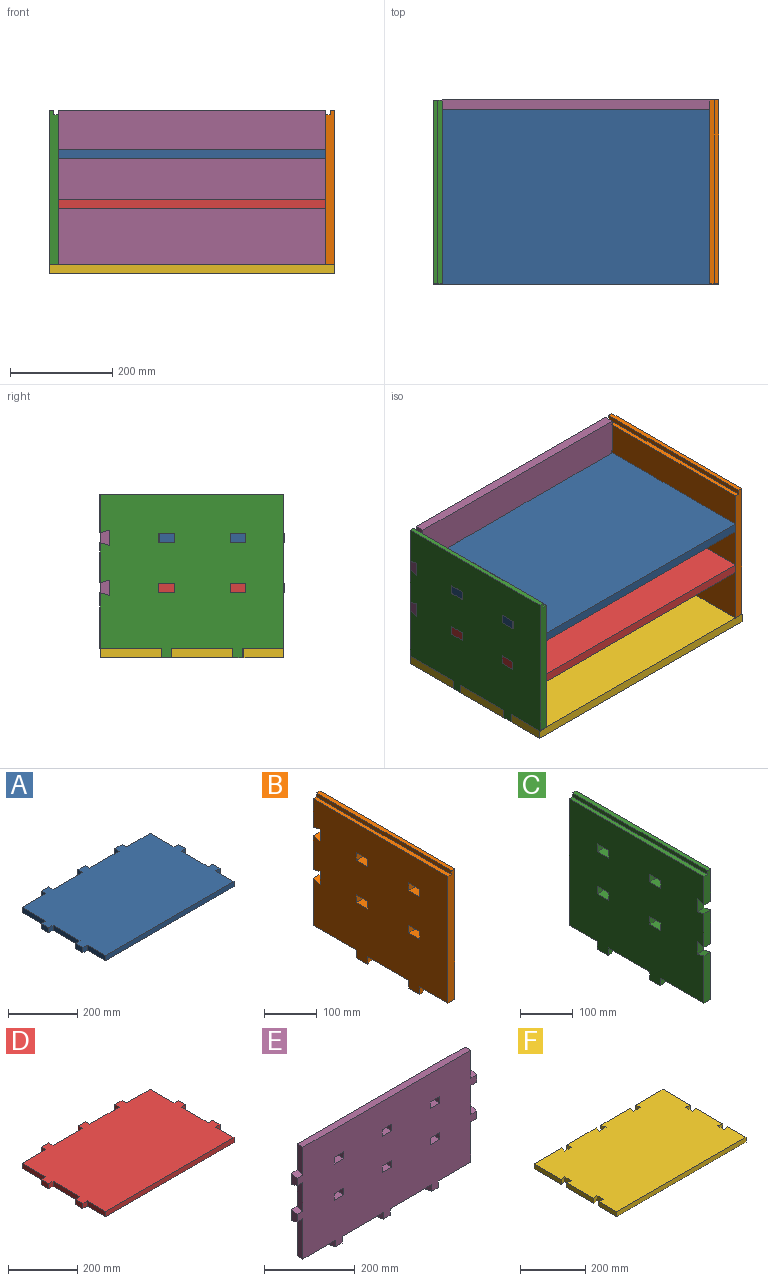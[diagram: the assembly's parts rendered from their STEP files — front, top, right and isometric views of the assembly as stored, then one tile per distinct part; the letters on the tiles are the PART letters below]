
ASSEMBLY  parts=6 mates=5
PART A: 34 faces, bbox 560x360.5x18 mm
  f0: plane 30x18mm, normal (0,1,0), area 540mm2, adj f1,f31,f32,f33
  f1: plane 18x18mm, normal (-1,0,0), area 324mm2, adj f0,f2,f32,f33
  f2: plane 120x18mm, normal (0,1,0), area 2160mm2, adj f1,f3,f32,f33
  f3: plane 18x18mm, normal (1,0,0), area 324mm2, adj f2,f4,f32,f33
  f4: plane 30x18mm, normal (0,1,0), area 540mm2, adj f3,f5,f32,f33
  f5: plane 18x18mm, normal (-1,0,0), area 324mm2, adj f4,f6,f32,f33
  f6: plane 97x18mm, normal (0,1,0), area 1746mm2, adj f5,f7,f32,f33
  f7: plane 97x18mm, normal (-1,0,0), area 1746mm2, adj f6,f8,f32,f33
  f8: plane 18x18mm, normal (0,1,0), area 324mm2, adj f7,f9,f32,f33
  f9: plane 30x18mm, normal (-1,0,0), area 540mm2, adj f8,f10,f32,f33
  f10: plane 18x18mm, normal (0,-1,0), area 324mm2, adj f9,f11,f32,f33
  f11: plane 110x18mm, normal (-1,0,0), area 1980mm2, adj f10,f12,f32,f33
  f12: plane 18x18mm, normal (0,1,0), area 324mm2, adj f11,f13,f32,f33
  f13: plane 30x18mm, normal (-1,0,0), area 540mm2, adj f12,f14,f32,f33
  f14: plane 18x18mm, normal (0,-1,0), area 324mm2, adj f13,f15,f32,f33
  f15: plane 75x18mm, normal (-1,0,0), area 1350mm2, adj f14,f16,f32,f33
  f16: plane 524x18mm, normal (0,-1,0), area 9432mm2, adj f15,f17,f32,f33
  f17: plane 75x18mm, normal (1,0,0), area 1350mm2, adj f16,f18,f32,f33
  f18: plane 18x18mm, normal (0,-1,0), area 324mm2, adj f17,f19,f32,f33
  f19: plane 30.58x18mm, normal (1,0,0), area 550.4mm2, adj f18,f20,f32,f33
  f20: plane 18x18mm, normal (0,1,0), area 324mm2, adj f19,f21,f32,f33
  f21: plane 110x18mm, normal (1,0,0), area 1980mm2, adj f20,f22,f32,f33
  f22: plane 18x18mm, normal (0,-1,0), area 324mm2, adj f21,f23,f32,f33
  f23: plane 29.42x18mm, normal (1,0,0), area 529.6mm2, adj f22,f24,f32,f33
  f24: plane 18x18mm, normal (0,1,0), area 324mm2, adj f23,f25,f32,f33
  f25: plane 97x18mm, normal (1,0,0), area 1746mm2, adj f24,f26,f32,f33
  f26: plane 97x18mm, normal (0,1,0), area 1746mm2, adj f25,f27,f32,f33
  f27: plane 18x18mm, normal (1,0,0), area 324mm2, adj f26,f28,f32,f33
  f28: plane 30x18mm, normal (0,1,0), area 540mm2, adj f27,f29,f32,f33
  f29: plane 18x17.51mm, normal (-1,0,0), area 315.2mm2, adj f28,f30,f32,f33
  f30: plane 120x18mm, normal (0,1,0), area 2160mm2, adj f29,f31,f32,f33
  f31: plane 18x18mm, normal (1,0,0), area 324mm2, adj f0,f30,f32,f33
  f32: plane 560x360.49mm, normal (0,0,1), area 183091.1mm2, adj f0,f1,f2,f3,f4,f5,f6,f7
  f33: plane 560x360.49mm, normal (0,0,-1), area 183091.1mm2, adj f0,f1,f2,f3,f4,f5,f6,f7
PART B: 40 faces, bbox 18x360x320 mm
  f0: plane 360x320mm, normal (1,0,0), area 106380mm2, adj f1,f3,f4,f5,f6,f7,f8,f9
  f1: plane 18x18mm, normal (0.27,0.96,0), area 336.3mm2, adj f0,f2,f4,f5
  f2: plane 360x311mm, normal (-1,0,0), area 103500mm2, adj f1,f3,f4,f5,f6,f7,f8,f9
  f3: plane 18x18mm, normal (0.27,-0.96,0), area 336.3mm2, adj f0,f2,f4,f9
  f4: plane 30x18mm, normal (0,0,-1), area 450mm2, adj f0,f1,f2,f3
  f5: plane 120x18mm, normal (0,0,-1), area 2115mm2, adj f0,f1,f2,f15
  f6: plane 18x18mm, normal (0.27,-0.96,0), area 336.3mm2, adj f0,f2,f8,f14
  f7: plane 18x18mm, normal (0.27,0.96,0), area 336.3mm2, adj f0,f2,f8,f9
  f8: plane 30x18mm, normal (0,0,-1), area 450mm2, adj f0,f2,f6,f7
  f9: plane 120x18mm, normal (0,0,-1), area 2070mm2, adj f0,f2,f3,f7
  f10: plane 360x9mm, normal (0,0,1), area 3240mm2, adj f0,f23,f33,f39
  f11: plane 18x18mm, normal (0,1,0), area 324mm2, adj f0,f2,f12,f37
  f12: plane 30x18mm, normal (0,0,-1), area 540mm2, adj f0,f2,f11,f13
  f13: plane 18x18mm, normal (0,-1,0), area 324mm2, adj f0,f2,f12,f37
  f14: plane 80x18mm, normal (0,0,-1), area 1395mm2, adj f0,f2,f6,f33
  f15: plane 109x18mm, normal (0,1,0), area 1962mm2, adj f0,f2,f5,f16
  f16: plane 18x18mm, normal (0,-0.27,0.96), area 336.3mm2, adj f0,f2,f15,f17
  f17: plane 30x18mm, normal (0,1,0), area 540mm2, adj f0,f2,f16,f18
  f18: plane 18x18mm, normal (0,-0.27,-0.96), area 336.3mm2, adj f0,f2,f17,f19
  f19: plane 78x18mm, normal (0,1,0), area 1404mm2, adj f0,f2,f18,f20
  f20: plane 18x18mm, normal (0,-0.27,0.96), area 336.3mm2, adj f0,f2,f19,f21
  f21: plane 30x18mm, normal (0,1,0), area 540mm2, adj f0,f2,f20,f22
  f22: plane 18x18mm, normal (0,-0.27,-0.96), area 336.3mm2, adj f0,f2,f21,f23
  f23: plane 75x18mm, normal (0,1,0), area 1269mm2, adj f0,f2,f10,f22,f38,f39
  f24: plane 18x18mm, normal (0,1,0), area 324mm2, adj f0,f2,f25,f34
  f25: plane 30x18mm, normal (0,0,-1), area 540mm2, adj f0,f2,f24,f26
  f26: plane 18x18mm, normal (0,-1,0), area 324mm2, adj f0,f2,f25,f34
  f27: plane 30x18mm, normal (0,0,1), area 540mm2, adj f0,f2,f28,f35
  f28: plane 18x18mm, normal (0,1,0), area 324mm2, adj f0,f2,f27,f29
  f29: plane 30x18mm, normal (0,0,-1), area 540mm2, adj f0,f2,f28,f35
  f30: plane 30x18mm, normal (0,0,-1), area 540mm2, adj f0,f2,f31,f36
  f31: plane 18x18mm, normal (0,-1,0), area 324mm2, adj f0,f2,f30,f32
  f32: plane 30x18mm, normal (0,0,1), area 540mm2, adj f0,f2,f31,f36
  f33: plane 302x18mm, normal (0,-1,0), area 5355mm2, adj f0,f2,f10,f14,f38,f39
  f34: plane 30x18mm, normal (0,0,1), area 540mm2, adj f0,f2,f24,f26
  f35: plane 18x18mm, normal (0,-1,0), area 324mm2, adj f0,f2,f27,f29
  f36: plane 18x18mm, normal (0,1,0), area 324mm2, adj f0,f2,f30,f32
  f37: plane 30x18mm, normal (0,0,1), area 540mm2, adj f0,f2,f11,f13
  f38: plane 360x9mm, normal (0,0,1), area 3240mm2, adj f2,f23,f33,f39
  f39: plane 360x9mm, normal (-1,0,0), area 3240mm2, adj f10,f23,f33,f38
PART C: 40 faces, bbox 18x360x320 mm
  f0: plane 360x320mm, normal (1,0,0), area 106380mm2, adj f1,f3,f4,f5,f6,f7,f8,f9
  f1: plane 18x18mm, normal (0.27,0.96,0), area 336.3mm2, adj f0,f2,f4,f5
  f2: plane 360x311mm, normal (-1,0,0), area 103500mm2, adj f1,f3,f4,f5,f6,f7,f8,f9
  f3: plane 18x18mm, normal (0.27,-0.96,0), area 336.3mm2, adj f0,f2,f4,f9
  f4: plane 30x18mm, normal (0,0,-1), area 450mm2, adj f0,f1,f2,f3
  f5: plane 80x18mm, normal (0,0,-1), area 1395mm2, adj f0,f1,f2,f10
  f6: plane 18x18mm, normal (0.27,-0.96,0), area 336.3mm2, adj f0,f2,f8,f19
  f7: plane 18x18mm, normal (0.27,0.96,0), area 336.3mm2, adj f0,f2,f8,f9
  f8: plane 30x18mm, normal (0,0,-1), area 450mm2, adj f0,f2,f6,f7
  f9: plane 120x18mm, normal (0,0,-1), area 2070mm2, adj f0,f2,f3,f7
  f10: plane 302x18mm, normal (0,1,0), area 5355mm2, adj f0,f2,f5,f11,f38,f39
  f11: plane 360x9mm, normal (0,0,1), area 3240mm2, adj f0,f10,f20,f39
  f12: plane 30x18mm, normal (0,-1,0), area 540mm2, adj f0,f2,f13,f37
  f13: plane 18x18mm, normal (0,0.27,0.96), area 336.3mm2, adj f0,f2,f12,f14
  f14: plane 78x18mm, normal (0,-1,0), area 1404mm2, adj f0,f2,f13,f15
  f15: plane 18x18mm, normal (0,0.27,-0.96), area 336.3mm2, adj f0,f2,f14,f16
  f16: plane 30x18mm, normal (0,-1,0), area 540mm2, adj f0,f2,f15,f17
  f17: plane 18x18mm, normal (0,0.27,0.96), area 336.3mm2, adj f0,f2,f16,f18
  f18: plane 109x18mm, normal (0,-1,0), area 1962mm2, adj f0,f2,f17,f19
  f19: plane 120x18mm, normal (0,0,-1), area 2115mm2, adj f0,f2,f6,f18
  f20: plane 75x18mm, normal (0,-1,0), area 1269mm2, adj f0,f2,f11,f37,f38,f39
  f21: plane 18x18mm, normal (0,1,0), area 324mm2, adj f0,f2,f22,f33
  f22: plane 30x18mm, normal (0,0,-1), area 540mm2, adj f0,f2,f21,f23
  f23: plane 18x18mm, normal (0,-1,0), area 324mm2, adj f0,f2,f22,f33
  f24: plane 18x18mm, normal (0,1,0), area 324mm2, adj f0,f2,f25,f34
  f25: plane 30x18mm, normal (0,0,-1), area 540mm2, adj f0,f2,f24,f26
  f26: plane 18x18mm, normal (0,-1,0), area 324mm2, adj f0,f2,f25,f34
  f27: plane 30x18mm, normal (0,0,1), area 540mm2, adj f0,f2,f28,f35
  f28: plane 18x18mm, normal (0,1,0), area 324mm2, adj f0,f2,f27,f29
  f29: plane 30x18mm, normal (0,0,-1), area 540mm2, adj f0,f2,f28,f35
  f30: plane 30x18mm, normal (0,0,-1), area 540mm2, adj f0,f2,f31,f36
  f31: plane 18x18mm, normal (0,-1,0), area 324mm2, adj f0,f2,f30,f32
  f32: plane 30x18mm, normal (0,0,1), area 540mm2, adj f0,f2,f31,f36
  f33: plane 30x18mm, normal (0,0,1), area 540mm2, adj f0,f2,f21,f23
  f34: plane 30x18mm, normal (0,0,1), area 540mm2, adj f0,f2,f24,f26
  f35: plane 18x18mm, normal (0,-1,0), area 324mm2, adj f0,f2,f27,f29
  f36: plane 18x18mm, normal (0,1,0), area 324mm2, adj f0,f2,f30,f32
  f37: plane 18x18mm, normal (0,0.27,-0.96), area 336.3mm2, adj f0,f2,f12,f20
  f38: plane 360x9mm, normal (0,0,1), area 3240mm2, adj f2,f10,f20,f39
  f39: plane 360x9mm, normal (-1,0,0), area 3240mm2, adj f10,f11,f20,f38
PART D: 34 faces, bbox 560x360.5x18 mm
  f0: plane 30x18mm, normal (0,1,0), area 540mm2, adj f1,f31,f32,f33
  f1: plane 18x18mm, normal (-1,0,0), area 324mm2, adj f0,f2,f32,f33
  f2: plane 120x18mm, normal (0,1,0), area 2160mm2, adj f1,f3,f32,f33
  f3: plane 18x18mm, normal (1,0,0), area 324mm2, adj f2,f4,f32,f33
  f4: plane 30x18mm, normal (0,1,0), area 540mm2, adj f3,f5,f32,f33
  f5: plane 18x18mm, normal (-1,0,0), area 324mm2, adj f4,f6,f32,f33
  f6: plane 97x18mm, normal (0,1,0), area 1746mm2, adj f5,f7,f32,f33
  f7: plane 97x18mm, normal (-1,0,0), area 1746mm2, adj f6,f8,f32,f33
  f8: plane 18x18mm, normal (0,1,0), area 324mm2, adj f7,f9,f32,f33
  f9: plane 30x18mm, normal (-1,0,0), area 540mm2, adj f8,f10,f32,f33
  f10: plane 18x18mm, normal (0,-1,0), area 324mm2, adj f9,f11,f32,f33
  f11: plane 110x18mm, normal (-1,0,0), area 1980mm2, adj f10,f12,f32,f33
  f12: plane 18x18mm, normal (0,1,0), area 324mm2, adj f11,f13,f32,f33
  f13: plane 29.99x18mm, normal (-1,0,0), area 539.7mm2, adj f12,f14,f32,f33
  f14: plane 18x18mm, normal (0,-1,0), area 324mm2, adj f13,f15,f32,f33
  f15: plane 75.51x18mm, normal (-1,0,0), area 1359.1mm2, adj f14,f16,f32,f33
  f16: plane 524x18mm, normal (0,-1,0), area 9432mm2, adj f15,f17,f32,f33
  f17: plane 75x18mm, normal (1,0,0), area 1350mm2, adj f16,f18,f32,f33
  f18: plane 18x18mm, normal (0,-1,0), area 324mm2, adj f17,f19,f32,f33
  f19: plane 30.58x18mm, normal (1,0,0), area 550.4mm2, adj f18,f20,f32,f33
  f20: plane 18x18mm, normal (0,1,0), area 324mm2, adj f19,f21,f32,f33
  f21: plane 110x18mm, normal (1,0,0), area 1980mm2, adj f20,f22,f32,f33
  f22: plane 18x18mm, normal (0,-1,0), area 324mm2, adj f21,f23,f32,f33
  f23: plane 29.91x18mm, normal (1,0,0), area 538.4mm2, adj f22,f24,f32,f33
  f24: plane 18x18mm, normal (0,1,0), area 324mm2, adj f23,f25,f32,f33
  f25: plane 97x18mm, normal (1,0,0), area 1746mm2, adj f24,f26,f32,f33
  f26: plane 97x18mm, normal (0,1,0), area 1746mm2, adj f25,f27,f32,f33
  f27: plane 18x18mm, normal (1,0,0), area 324mm2, adj f26,f28,f32,f33
  f28: plane 30x18mm, normal (0,1,0), area 540mm2, adj f27,f29,f32,f33
  f29: plane 18x18mm, normal (-1,0,0), area 324mm2, adj f28,f30,f32,f33
  f30: plane 120x18mm, normal (0,1,0), area 2160mm2, adj f29,f31,f32,f33
  f31: plane 18x18mm, normal (1,0,0), area 324mm2, adj f0,f30,f32,f33
  f32: plane 560x360.49mm, normal (0,0,1), area 183253.8mm2, adj f0,f1,f2,f3,f4,f5,f6,f7
  f33: plane 560x360.49mm, normal (0,0,-1), area 183253.8mm2, adj f0,f1,f2,f3,f4,f5,f6,f7
PART E: 58 faces, bbox 560x18x320 mm
  f0: plane 78x18mm, normal (1,0,0), area 1314mm2, adj f35,f36,f54,f55
  f1: plane 109x18mm, normal (1,0,0), area 1917mm2, adj f8,f35,f36,f56
  f2: plane 78x18mm, normal (-1,0,0), area 1314mm2, adj f35,f36,f46,f49
  f3: plane 109x18mm, normal (-1,0,0), area 1917mm2, adj f4,f35,f36,f50
  f4: plane 102x18mm, normal (0,0,-1), area 1791mm2, adj f3,f35,f36,f43
  f5: plane 130x18mm, normal (0,0,-1), area 2250mm2, adj f35,f36,f38,f40
  f6: plane 130x18mm, normal (0,0,-1), area 2250mm2, adj f35,f36,f37,f44
  f7: plane 75x18mm, normal (-1,0,0), area 1305mm2, adj f34,f35,f36,f47
  f8: plane 102x18mm, normal (0,0,-1), area 1791mm2, adj f1,f35,f36,f41
  f9: plane 75x18mm, normal (1,0,0), area 1305mm2, adj f34,f35,f36,f53
  f10: plane 18x18mm, normal (1,0,0), area 324mm2, adj f11,f28,f35,f36
  f11: plane 30x18mm, normal (0,0,-1), area 540mm2, adj f10,f12,f35,f36
  f12: plane 18x18mm, normal (-1,0,0), area 324mm2, adj f11,f28,f35,f36
  f13: plane 18x18mm, normal (1,0,0), area 324mm2, adj f14,f29,f35,f36
  f14: plane 30x18mm, normal (0,0,-1), area 540mm2, adj f13,f15,f35,f36
  f15: plane 18x18mm, normal (-1,0,0), area 324mm2, adj f14,f29,f35,f36
  f16: plane 18x18mm, normal (1,0,0), area 324mm2, adj f17,f30,f35,f36
  f17: plane 30x18mm, normal (0,0,-1), area 540mm2, adj f16,f18,f35,f36
  f18: plane 18x18mm, normal (-1,0,0), area 324mm2, adj f17,f30,f35,f36
  f19: plane 18x18mm, normal (1,0,0), area 324mm2, adj f20,f31,f35,f36
  f20: plane 30x18mm, normal (0,0,-1), area 540mm2, adj f19,f21,f35,f36
  f21: plane 18x18mm, normal (-1,0,0), area 324mm2, adj f20,f31,f35,f36
  f22: plane 18x18mm, normal (-1,0,0), area 324mm2, adj f23,f32,f35,f36
  f23: plane 30x18mm, normal (0,0,1), area 540mm2, adj f22,f24,f35,f36
  f24: plane 18x18mm, normal (1,0,0), area 324mm2, adj f23,f32,f35,f36
  f25: plane 18x18mm, normal (-1,0,0), area 324mm2, adj f26,f33,f35,f36
  f26: plane 30x18mm, normal (0,0,1), area 540mm2, adj f25,f27,f35,f36
  f27: plane 18x18mm, normal (1,0,0), area 324mm2, adj f26,f33,f35,f36
  f28: plane 30x18mm, normal (0,0,1), area 540mm2, adj f10,f12,f35,f36
  f29: plane 30x18mm, normal (0,0,1), area 540mm2, adj f13,f15,f35,f36
  f30: plane 30x18mm, normal (0,0,1), area 540mm2, adj f16,f18,f35,f36
  f31: plane 30x18mm, normal (0,0,1), area 540mm2, adj f19,f21,f35,f36
  f32: plane 30x18mm, normal (0,0,-1), area 540mm2, adj f22,f24,f35,f36
  f33: plane 30x18mm, normal (0,0,-1), area 540mm2, adj f25,f27,f35,f36
  f34: plane 524x18mm, normal (0,0,1), area 9432mm2, adj f7,f9,f35,f36
  f35: plane 560x320mm, normal (0,-1,0), area 157528mm2, adj f0,f1,f2,f3,f4,f5,f6,f7
  f36: plane 560x320mm, normal (0,1,0), area 158788mm2, adj f0,f1,f2,f3,f4,f5,f6,f7
  f37: plane 18x18mm, normal (-0.96,-0.27,0), area 336.3mm2, adj f6,f35,f36,f39
  f38: plane 18x18mm, normal (0.96,-0.27,0), area 336.3mm2, adj f5,f35,f36,f39
  f39: plane 30x18mm, normal (0,0,-1), area 450mm2, adj f35,f36,f37,f38
  f40: plane 18x18mm, normal (-0.96,-0.27,0), area 336.3mm2, adj f5,f35,f36,f42
  f41: plane 18x18mm, normal (0.96,-0.27,0), area 336.3mm2, adj f8,f35,f36,f42
  f42: plane 30x18mm, normal (0,0,-1), area 450mm2, adj f35,f36,f40,f41
  f43: plane 18x18mm, normal (-0.96,-0.27,0), area 336.3mm2, adj f4,f35,f36,f45
  f44: plane 18x18mm, normal (0.96,-0.27,0), area 336.3mm2, adj f6,f35,f36,f45
  f45: plane 30x18mm, normal (0,0,-1), area 450mm2, adj f35,f36,f43,f44
  f46: plane 18x18mm, normal (0,-0.27,-0.96), area 336.3mm2, adj f2,f35,f36,f48
  f47: plane 18x18mm, normal (0,-0.27,0.96), area 336.3mm2, adj f7,f35,f36,f48
  f48: plane 30x18mm, normal (-1,0,0), area 450mm2, adj f35,f36,f46,f47
  f49: plane 18x18mm, normal (0,-0.27,0.96), area 336.3mm2, adj f2,f35,f36,f51
  f50: plane 18x18mm, normal (0,-0.27,-0.96), area 336.3mm2, adj f3,f35,f36,f51
  f51: plane 30x18mm, normal (-1,0,0), area 450mm2, adj f35,f36,f49,f50
  f52: plane 30x18mm, normal (1,0,0), area 450mm2, adj f35,f36,f53,f54
  f53: plane 18x18mm, normal (0,-0.27,0.96), area 336.3mm2, adj f9,f35,f36,f52
  f54: plane 18x18mm, normal (0,-0.27,-0.96), area 336.3mm2, adj f0,f35,f36,f52
  f55: plane 18x18mm, normal (0,-0.27,0.96), area 336.3mm2, adj f0,f35,f36,f57
  f56: plane 18x18mm, normal (0,-0.27,-0.96), area 336.3mm2, adj f1,f35,f36,f57
  f57: plane 30x18mm, normal (1,0,0), area 450mm2, adj f35,f36,f55,f56
PART F: 34 faces, bbox 560x360x18 mm
  f0: plane 30x18mm, normal (0,1,0), area 540mm2, adj f1,f31,f32,f33
  f1: plane 18x18mm, normal (0.96,-0.27,0), area 336.3mm2, adj f0,f2,f32,f33
  f2: plane 130x18mm, normal (0,1,0), area 2340mm2, adj f1,f3,f32,f33
  f3: plane 18x18mm, normal (-0.96,-0.27,0), area 336.3mm2, adj f2,f4,f32,f33
  f4: plane 30x18mm, normal (0,1,0), area 540mm2, adj f3,f5,f32,f33
  f5: plane 18x18mm, normal (0.96,-0.27,0), area 336.3mm2, adj f4,f6,f32,f33
  f6: plane 120x18mm, normal (0,1,0), area 2160mm2, adj f5,f7,f32,f33
  f7: plane 120x18mm, normal (-1,0,0), area 2160mm2, adj f6,f8,f32,f33
  f8: plane 18x18mm, normal (0.27,-0.96,0), area 336.3mm2, adj f7,f9,f32,f33
  f9: plane 30x18mm, normal (-1,0,0), area 540mm2, adj f8,f10,f32,f33
  f10: plane 18x18mm, normal (0.27,0.96,0), area 336.3mm2, adj f9,f11,f32,f33
  f11: plane 120x18mm, normal (-1,0,0), area 2160mm2, adj f10,f12,f32,f33
  f12: plane 18x18mm, normal (0.27,-0.96,0), area 336.3mm2, adj f11,f13,f32,f33
  f13: plane 30x18mm, normal (-1,0,0), area 540mm2, adj f12,f14,f32,f33
  f14: plane 18x18mm, normal (0.27,0.96,0), area 336.3mm2, adj f13,f15,f32,f33
  f15: plane 80x18mm, normal (-1,0,0), area 1440mm2, adj f14,f16,f32,f33
  f16: plane 560x18mm, normal (0,-1,0), area 10080mm2, adj f15,f17,f32,f33
  f17: plane 80x18mm, normal (1,0,0), area 1440mm2, adj f16,f18,f32,f33
  f18: plane 18x18mm, normal (-0.27,0.96,0), area 336.3mm2, adj f17,f19,f32,f33
  f19: plane 30x18mm, normal (1,0,0), area 540mm2, adj f18,f20,f32,f33
  f20: plane 18x18mm, normal (-0.27,-0.96,0), area 336.3mm2, adj f19,f21,f32,f33
  f21: plane 120x18mm, normal (1,0,0), area 2160mm2, adj f20,f22,f32,f33
  f22: plane 18x18mm, normal (-0.27,0.96,0), area 336.3mm2, adj f21,f23,f32,f33
  f23: plane 30x18mm, normal (1,0,0), area 540mm2, adj f22,f24,f32,f33
  f24: plane 18x18mm, normal (-0.27,-0.96,0), area 336.3mm2, adj f23,f25,f32,f33
  f25: plane 120x18mm, normal (1,0,0), area 2160mm2, adj f24,f26,f32,f33
  f26: plane 120x18mm, normal (0,1,0), area 2160mm2, adj f25,f27,f32,f33
  f27: plane 18x18mm, normal (-0.96,-0.27,0), area 336.3mm2, adj f26,f28,f32,f33
  f28: plane 30x18mm, normal (0,1,0), area 540mm2, adj f27,f29,f32,f33
  f29: plane 18x18mm, normal (0.96,-0.27,0), area 336.3mm2, adj f28,f30,f32,f33
  f30: plane 130x18mm, normal (0,1,0), area 2340mm2, adj f29,f31,f32,f33
  f31: plane 18x18mm, normal (-0.96,-0.27,0), area 336.3mm2, adj f0,f30,f32,f33
  f32: plane 560x360mm, normal (0,0,1), area 198450mm2, adj f0,f1,f2,f3,f4,f5,f6,f7
  f33: plane 560x360mm, normal (0,0,-1), area 198450mm2, adj f0,f1,f2,f3,f4,f5,f6,f7
PLACE A t=(341.82,-419.78,-122.2)mm
PLACE B t=(26.26,-145.17,-348.2)mm
PLACE C rot(axis=(0,0,-1),180deg) t=(65.3,-294.39,-348.2)mm
PLACE D t=(341.82,-419.78,-220.2)mm
PLACE E rot(axis=(0,0,-1),180deg) t=(-234.22,-37.78,-348.2)mm
PLACE F t=(365.78,-419.78,-348.2)mm fixed
MATE slider A.f14 <-> C.f31  axis (0,-1,0) through (-234.15,-305.27,-122.2)mm
MATE slider C.f6 <-> F.f8  axis (-0.27,0.96,0) through (-234.15,-140.03,-348.2)mm
MATE slider E.f37 <-> F.f31  axis (0.96,0.27,0) through (60.78,-37.78,-348.2)mm
MATE slider B.f6 <-> F.f18  axis (0.27,-0.96,0) through (316.71,-302.03,-339.2)mm
MATE slider D.f14 <-> C.f26  axis (0,-1,0) through (-234.15,-304.76,-220.2)mm
